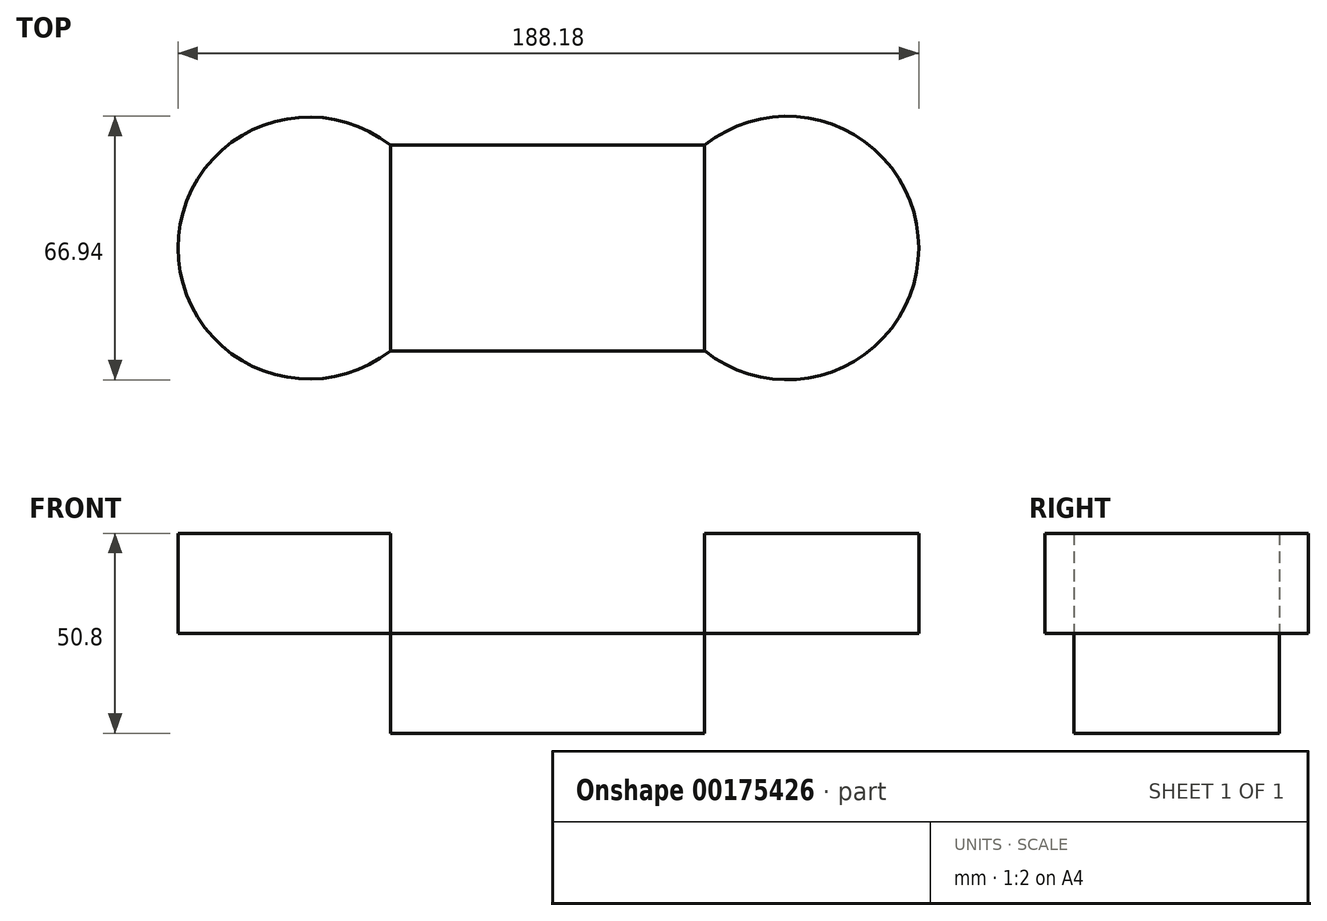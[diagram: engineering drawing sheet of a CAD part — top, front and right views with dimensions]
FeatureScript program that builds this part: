
annotation { "Feature Type Name" : "Feature", "Feature Type Description" : "" }
export const myFeature = defineFeature(function(context is Context, id is Id, definition is map)
    precondition{}
    {
        {
            var Q0;
            Q0=qCreatedBy(makeId("Top.planeOp"),FACE);
            var sketch = newSketch(context, id + "F0", { "sketchPlane" : qUnion([Q0])});
            skLineSegment(sketch, "E0.bottom", {"start": v(39.91, -26.1) * mm, "end": v(-39.91, -26.1) * mm});
            skLineSegment(sketch, "E0.top", {"start": v(39.91, 26.1) * mm, "end": v(-39.91, 26.1) * mm});
            skLineSegment(sketch, "E0.left", {"start": v(39.91, -26.1) * mm, "end": v(39.91, 26.1) * mm});
            skLineSegment(sketch, "E0.right", {"start": v(-39.91, -26.1) * mm, "end": v(-39.91, 26.1) * mm});
            skPoint(sketch, "E0.middle", {"position": v(0, 0) * mm});
            skSolve(sketch);
        }
        {
            var Q0;
            Q0 = qSketchRegion(id + "F0", true);
            extrude(context, id + "F1", {"entities" : qUnion([Q0]), "depth" : 25.4 * mm});
        }
        {
            var Q0;
            Q0=makeQuery(id+"F1.opExtrude","CAP_FACE",FACE,{"disambiguationData":[OSD([sQuery(id+"F0.wireOp",EDGE,"E0.bottom"),sQuery(id+"F0.wireOp",EDGE,"E0.top"),sQuery(id+"F0.wireOp",EDGE,"E0.left"),sQuery(id+"F0.wireOp",EDGE,"E0.right")])],"isStart":false});
            var sketch = newSketch(context, id + "F2", { "sketchPlane" : qUnion([Q0])});
            skArc(sketch, "E1", {"start": v(-39.91, 26.1) * mm, "mid": v(-93.85, 0) * mm, "end": v(-39.91, -26.1) * mm});
            skArc(sketch, "E2", {"start": v(39.91, 26.1) * mm, "mid": v(94.33, 0) * mm, "end": v(39.91, -26.1) * mm});
            skLineSegment(sketch, "E3", {"start": v(-39.91, 26.1) * mm, "end": v(-39.91, -26.1) * mm});
            skLineSegment(sketch, "E4", {"start": v(-40.83, 26.67) * mm, "end": v(-40.83, -26.8) * mm});
            skLineSegment(sketch, "E5", {"start": v(42.17, -22.96) * mm, "end": v(39.91, -26.1) * mm});
            skLineSegment(sketch, "E6", {"start": v(39.91, -26.1) * mm, "end": v(39.91, 26.1) * mm});
            skSolve(sketch);
        }
        {
            var Q0;
            Q0 = qSketchRegion(id + "F2", true);
            extrude(context, id + "F3", {"entities" : qUnion([Q0]), "operationType" : NewBodyOperationType.ADD, "depth" : 25.4 * mm});
        }
        {
            var Q0;
            Q0 = qSketchRegion(id + "F2", true);
            extrude(context, id + "F4", {"entities" : qUnion([Q0]), "depth" : 25.4 * mm});
        }
    });
